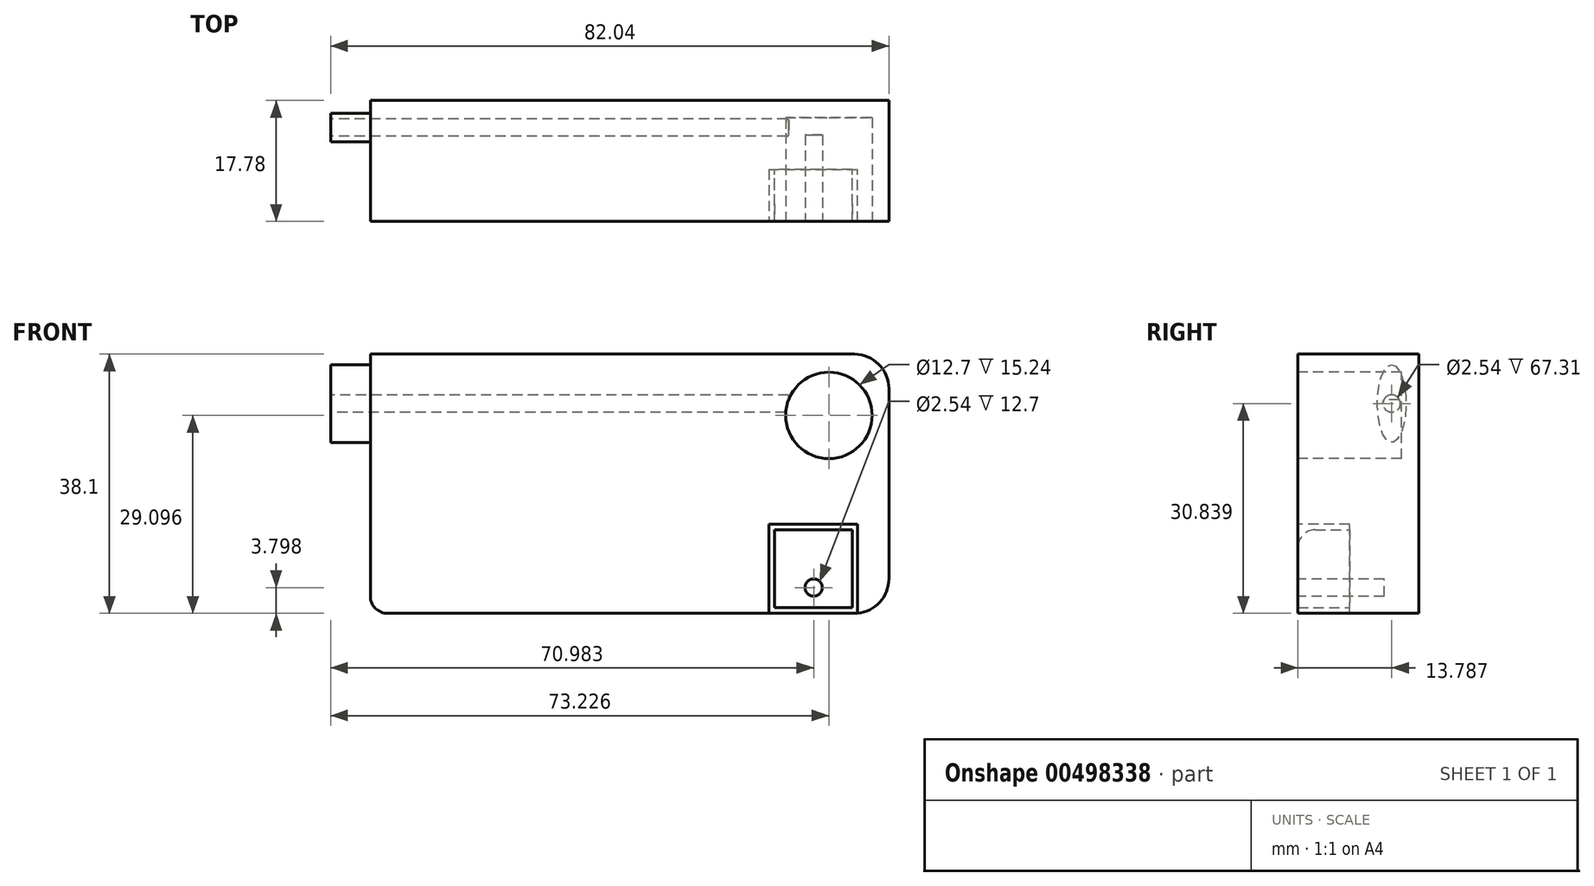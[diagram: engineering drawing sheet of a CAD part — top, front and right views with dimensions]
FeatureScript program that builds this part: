
annotation { "Feature Type Name" : "Feature", "Feature Type Description" : "" }
export const myFeature = defineFeature(function(context is Context, id is Id, definition is map)
    precondition{}
    {
        {
            var Q0;
            Q0=qCreatedBy(makeId("Front.planeOp"),FACE);
            var sketch = newSketch(context, id + "F0", { "sketchPlane" : qUnion([Q0])});
            skLineSegment(sketch, "E0.bottom", {"start": v(38.1, 19.05) * mm, "end": v(-38.1, 19.05) * mm});
            skLineSegment(sketch, "E0.top", {"start": v(38.1, -19.05) * mm, "end": v(-38.1, -19.05) * mm});
            skLineSegment(sketch, "E0.left", {"start": v(38.1, 19.05) * mm, "end": v(38.1, -19.05) * mm});
            skLineSegment(sketch, "E0.right", {"start": v(-38.1, 19.05) * mm, "end": v(-38.1, -19.05) * mm});
            skPoint(sketch, "E0.middle", {"position": v(0, 0) * mm});
            skSolve(sketch);
        }
        {
            var Q0;
            Q0 = qSketchRegion(id + "F0", true);
            extrude(context, id + "F1", {"entities" : qUnion([Q0]), "depth" : 17.78 * mm});
        }
        {
            var Q0;
            Q0=makeQuery(id+"F1.opExtrude","CAP_FACE",FACE,{"disambiguationData":[OSD([sQuery(id+"F0.wireOp",EDGE,"E0.bottom"),sQuery(id+"F0.wireOp",EDGE,"E0.top"),sQuery(id+"F0.wireOp",EDGE,"E0.left"),sQuery(id+"F0.wireOp",EDGE,"E0.right")])],"isStart":false});
            var sketch = newSketch(context, id + "F2", { "sketchPlane" : qUnion([Q0])});
            skCircle(sketch, "E1", {"center": v(29.29, 10.05) * mm, "radius": 6.35 * mm});
            skSolve(sketch);
        }
        {
            var Q0;
            Q0 = qSketchRegion(id + "F2", true);
            extrude(context, id + "F3", {"entities" : qUnion([Q0]), "operationType" : NewBodyOperationType.REMOVE, "oppositeDirection" : true, "depth" : 15.24 * mm});
        }
        {
            var Q0;
            Q0=makeQuery(id+"F1.opExtrude","SWEPT_FACE",FACE,{"disambiguationData":[OSD([sQuery(id+"F0.wireOp",EDGE,"E0.right")])]});
            var sketch = newSketch(context, id + "F4", { "sketchPlane" : qUnion([Q0])});
            skEllipse(sketch, "E2", {"center": v(4, 11.79) * mm, "majorRadius": 5.73 * mm, "minorRadius": 2.11 * mm, "majorAxis": v(0, 1)});
            skSolve(sketch);
        }
        {
            var Q0;
            Q0 = qSketchRegion(id + "F4", true);
            extrude(context, id + "F5", {"entities" : qUnion([Q0]), "operationType" : NewBodyOperationType.ADD, "depth" : 5.33 * mm});
        }
        {
            var Q0;
            Q0 = qSketchRegion(id + "F4", true);
            extrude(context, id + "F6", {"entities" : qUnion([Q0]), "operationType" : NewBodyOperationType.ADD, "depth" : 5.84 * mm});
        }
        {
            var Q0;
            Q0=makeQuery(id+"F6.opExtrude","CAP_FACE",FACE,{"disambiguationData":[OSD([sQuery(id+"F4.wireOp",EDGE,"E2")])],"isStart":false});
            var sketch = newSketch(context, id + "F7", { "sketchPlane" : qUnion([Q0])});
            skCircle(sketch, "E3", {"center": v(4, 11.79) * mm, "radius": 1.27 * mm});
            skSolve(sketch);
        }
        {
            var Q0;
            Q0=makeQuery(id+"F7.imprint","IMPRINT",FACE,{"disambiguationData":[TD([[makeQuery(id+"F7.imprint","IMPRINT",EDGE,{"derivedFrom":sQuery(id+"F7.wireOp",EDGE,"E3")}),1.0]])]});
            extrude(context, id + "F8", {"entities" : qUnion([Q0]), "operationType" : NewBodyOperationType.REMOVE, "oppositeDirection" : true, "depth" : 67.3 * mm});
        }
        {
            var Q0;
            Q0=makeQuery(id+"F1.opExtrude","SWEPT_EDGE",EDGE,{"disambiguationData":[OSD([sQuery(id+"F0.wireOp",EDGE,"E0.bottom"),sQuery(id+"F0.wireOp",EDGE,"E0.left")])]});
            fillet(context, id + "F9", {"entities" : qUnion([Q0]), "radius" : 5.08 * mm, "tangentPropagation" : true, "allowEdgeOverflow" : false});
        }
        {
            var Q0;
            Q0=makeQuery(id+"F1.opExtrude","SWEPT_EDGE",EDGE,{"disambiguationData":[OSD([sQuery(id+"F0.wireOp",EDGE,"E0.top"),sQuery(id+"F0.wireOp",EDGE,"E0.left")])]});
            fillet(context, id + "F10", {"entities" : qUnion([Q0]), "radius" : 5.08 * mm, "tangentPropagation" : true, "allowEdgeOverflow" : false});
        }
        {
            var Q0;
            Q0=makeQuery(id+"F1.opExtrude","CAP_FACE",FACE,{"disambiguationData":[OSD([sQuery(id+"F0.wireOp",EDGE,"E0.bottom"),sQuery(id+"F0.wireOp",EDGE,"E0.top"),sQuery(id+"F0.wireOp",EDGE,"E0.left"),sQuery(id+"F0.wireOp",EDGE,"E0.right")])],"isStart":false});
            var sketch = newSketch(context, id + "F11", { "sketchPlane" : qUnion([Q0])});
            skLineSegment(sketch, "E4.bottom", {"start": v(20.46, -19.05) * mm, "end": v(33.51, -19.05) * mm});
            skLineSegment(sketch, "E4.top", {"start": v(20.46, -5.96) * mm, "end": v(33.51, -5.96) * mm});
            skLineSegment(sketch, "E4.left", {"start": v(20.46, -19.05) * mm, "end": v(20.46, -5.96) * mm});
            skLineSegment(sketch, "E4.right", {"start": v(33.51, -19.05) * mm, "end": v(33.51, -5.96) * mm});
            skSolve(sketch);
        }
        {
            var Q0;
            Q0 = qSketchRegion(id + "F11", true);
            extrude(context, id + "F12", {"entities" : qUnion([Q0]), "operationType" : NewBodyOperationType.REMOVE, "oppositeDirection" : true, "depth" : 7.62 * mm});
        }
        {
            var Q0;
            Q0=makeQuery(id+"F12.boolean.opBoolean","COPY",FACE,{"derivedFrom":makeQuery(id+"F12.opExtrude","CAP_FACE",FACE,{"disambiguationData":[OSD([sQuery(id+"F11.wireOp",EDGE,"E4.bottom"),sQuery(id+"F11.wireOp",EDGE,"E4.top"),sQuery(id+"F11.wireOp",EDGE,"E4.left"),sQuery(id+"F11.wireOp",EDGE,"E4.right")])],"isStart":false})});
            var sketch = newSketch(context, id + "F13", { "sketchPlane" : qUnion([Q0])});
            skLineSegment(sketch, "E5.bottom", {"start": v(32.7, -6.8) * mm, "end": v(21.27, -6.8) * mm});
            skLineSegment(sketch, "E5.top", {"start": v(32.7, -18.22) * mm, "end": v(21.27, -18.22) * mm});
            skLineSegment(sketch, "E5.left", {"start": v(32.7, -6.8) * mm, "end": v(32.7, -18.22) * mm});
            skLineSegment(sketch, "E5.right", {"start": v(21.27, -6.8) * mm, "end": v(21.27, -18.22) * mm});
            skPoint(sketch, "E5.middle", {"position": v(26.98, -12.5) * mm});
            skPoint(sketch, "E5.middle.positionSnap0", {"position": v(20.46, -12.5) * mm});
            skPoint(sketch, "E5.middle.positionSnap1", {"position": v(26.98, -5.96) * mm});
            skPoint(sketch, "E5.centerSnap0", {"position": v(20.46, -12.5) * mm});
            skPoint(sketch, "E5.centerSnap1", {"position": v(26.98, -5.96) * mm});
            skSolve(sketch);
        }
        {
            var Q0;
            Q0 = qSketchRegion(id + "F13", true);
            extrude(context, id + "F14", {"entities" : qUnion([Q0]), "operationType" : NewBodyOperationType.ADD, "depth" : 7.62 * mm});
        }
        {
            var Q0;
            Q0=makeQuery(id+"F14.opExtrude","CAP_EDGE",EDGE,{"disambiguationData":[OSD([sQuery(id+"F13.wireOp",EDGE,"E5.bottom")])],"isStart":false});
            fillet(context, id + "F15", {"entities" : qUnion([Q0]), "radius" : 2.54 * mm, "tangentPropagation" : true, "allowEdgeOverflow" : false});
        }
        {
            var Q0;
            Q0=makeQuery(id+"F14.opExtrude","CAP_FACE",FACE,{"disambiguationData":[OSD([sQuery(id+"F13.wireOp",EDGE,"E5.bottom"),sQuery(id+"F13.wireOp",EDGE,"E5.top"),sQuery(id+"F13.wireOp",EDGE,"E5.left"),sQuery(id+"F13.wireOp",EDGE,"E5.right")])],"isStart":false});
            var sketch = newSketch(context, id + "F16", { "sketchPlane" : qUnion([Q0])});
            skCircle(sketch, "E6", {"center": v(27.04, -15.25) * mm, "radius": 1.27 * mm});
            skSolve(sketch);
        }
        {
            var Q0;
            Q0 = qSketchRegion(id + "F16", true);
            var Q1;
            Q1=makeQuery(id+"F16.imprint","IMPRINT",FACE,{"disambiguationData":[TD([[makeQuery(id+"F16.imprint","IMPRINT",EDGE,{"derivedFrom":sQuery(id+"F16.wireOp",EDGE,"E6")}),1.0]])]});
            extrude(context, id + "F17", {"entities" : qUnion([Q0, Q1]), "operationType" : NewBodyOperationType.REMOVE, "oppositeDirection" : true, "depth" : 12.7 * mm});
        }
        {
            var Q0;
            Q0=makeQuery(id+"F1.opExtrude","SWEPT_EDGE",EDGE,{"disambiguationData":[OSD([sQuery(id+"F0.wireOp",EDGE,"E0.top"),sQuery(id+"F0.wireOp",EDGE,"E0.right")])]});
            fillet(context, id + "F18", {"entities" : qUnion([Q0]), "radius" : 2.54 * mm, "tangentPropagation" : true, "allowEdgeOverflow" : false});
        }
    });
